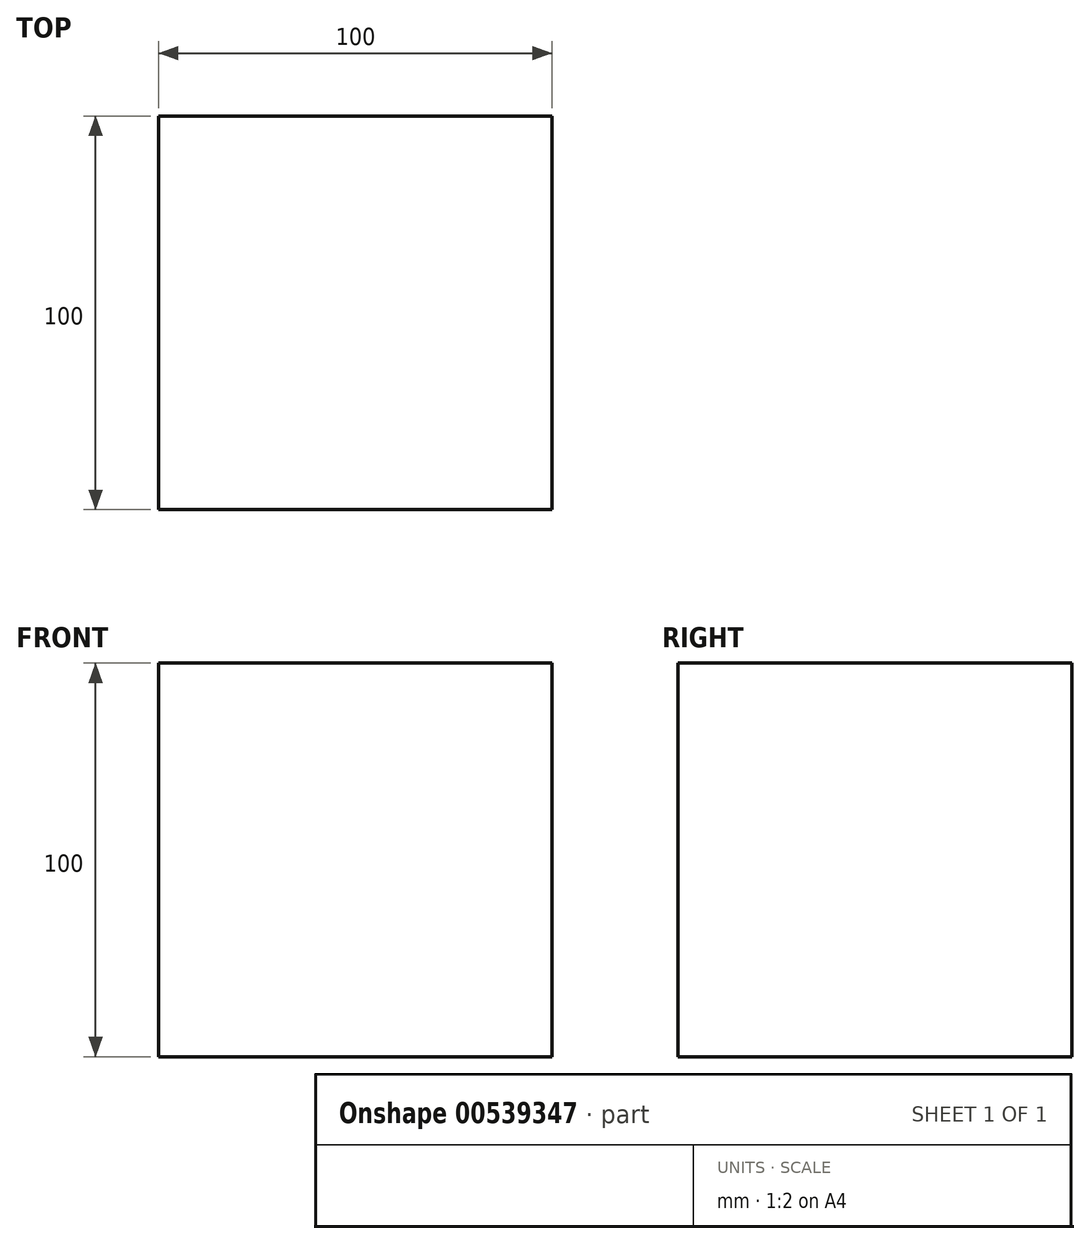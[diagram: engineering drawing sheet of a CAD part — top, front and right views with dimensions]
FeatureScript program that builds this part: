
annotation { "Feature Type Name" : "Feature", "Feature Type Description" : "" }
export const myFeature = defineFeature(function(context is Context, id is Id, definition is map)
    precondition{}
    {
        {
            var Q0;
            Q0=qCreatedBy(makeId("Top.planeOp"),FACE);
            var sketch = newSketch(context, id + "F0", { "sketchPlane" : qUnion([Q0])});
            skLineSegment(sketch, "E0.bottom", {"start": v(-50, 50) * mm, "end": v(50, 50) * mm});
            skLineSegment(sketch, "E0.top", {"start": v(-50, -50) * mm, "end": v(50, -50) * mm});
            skLineSegment(sketch, "E0.left", {"start": v(-50, 50) * mm, "end": v(-50, -50) * mm});
            skLineSegment(sketch, "E0.right", {"start": v(50, 50) * mm, "end": v(50, -50) * mm});
            skSolve(sketch);
        }
        {
            var Q0;
            Q0 = qSketchRegion(id + "F0", true);
            extrude(context, id + "F1", {"entities" : qUnion([Q0]), "depth" : 100 * mm, "offsetDistance" : 25 * mm});
        }
    });
